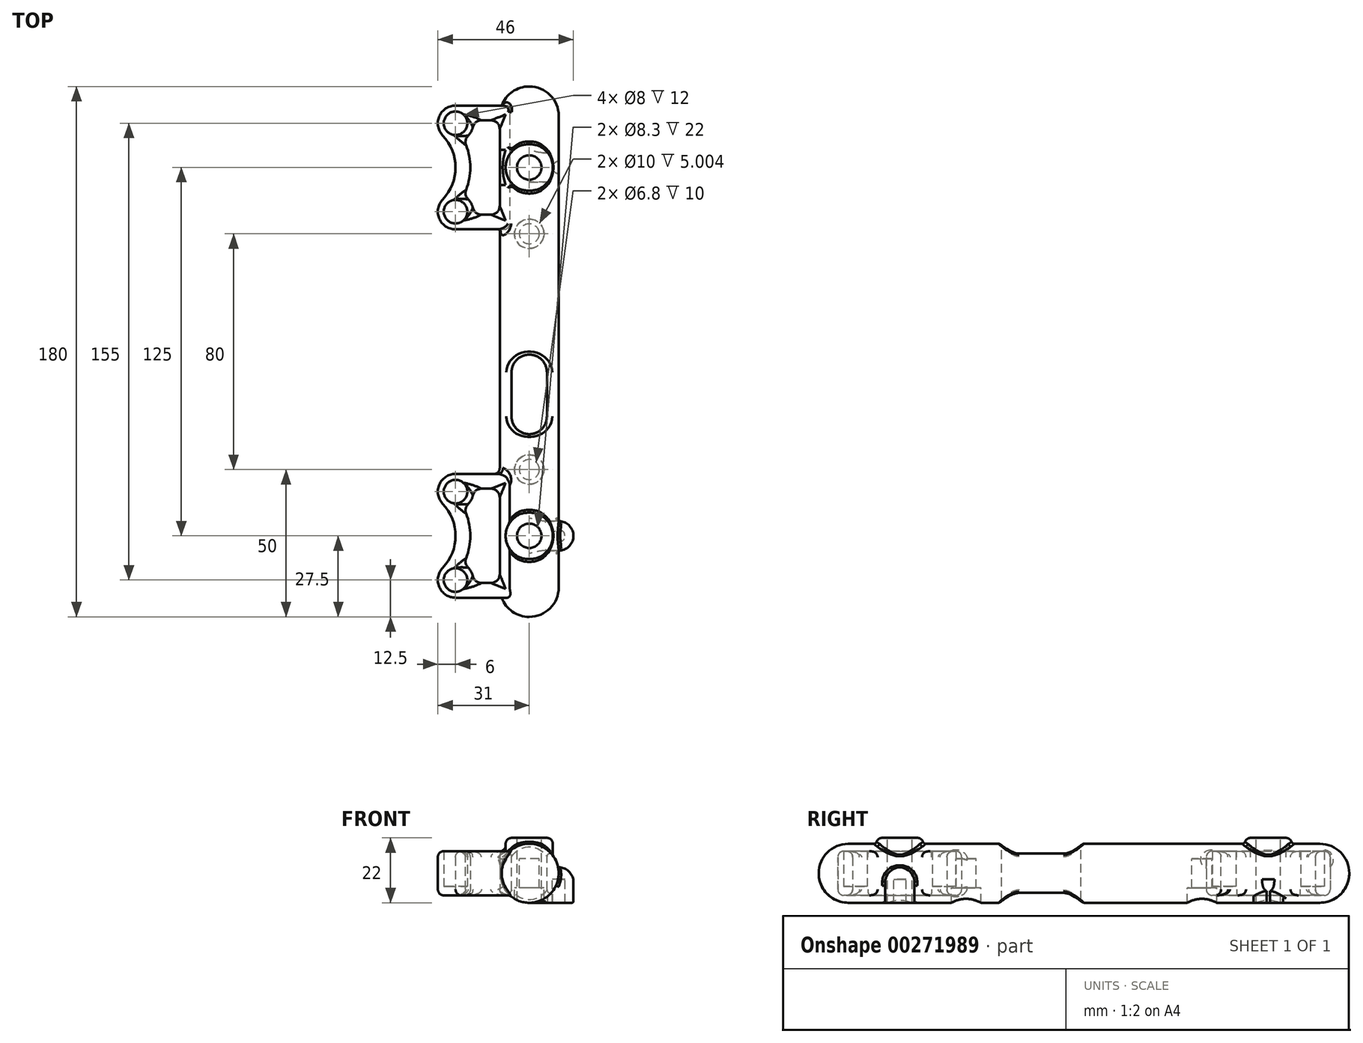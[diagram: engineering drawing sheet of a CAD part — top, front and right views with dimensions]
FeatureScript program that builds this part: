
annotation { "Feature Type Name" : "Feature", "Feature Type Description" : "" }
export const myFeature = defineFeature(function(context is Context, id is Id, definition is map)
    precondition{}
    {
        {
            var Q0;
            Q0=qCreatedBy(makeId("Front.planeOp"),FACE);
            var sketch = newSketch(context, id + "F0", { "sketchPlane" : qUnion([Q0])});
            skCircle(sketch, "E0", {"center": v(0, 0) * mm, "radius": 10 * mm});
            skSolve(sketch);
        }
        {
            var Q0;
            Q0=qCreatedBy(makeId("Right.planeOp"),FACE);
            var sketch = newSketch(context, id + "F1", { "sketchPlane" : qUnion([Q0])});
            skLineSegment(sketch, "E1", {"start": v(0, 0) * mm, "end": v(180, 0) * mm, "construction": true});
            skSolve(sketch);
        }
        {
            var Q0;
            Q0=qCreatedBy(makeId("Top.planeOp"),FACE);
            cPlane(context, id + "F2", {"entities" : qUnion([Q0]), "cplaneType" : CPlaneType.OFFSET, "offset" : 10 * mm, "oppositeDirection" : true, "width" : 150 * mm, "height" : 150 * mm});
        }
        {
            var Q0;
            Q0=qCreatedBy(id+"F2.planeOp",FACE);
            var sketch = newSketch(context, id + "F3", { "sketchPlane" : qUnion([Q0])});
            skLineSegment(sketch, "E2", {"start": v(0, 0) * mm, "end": v(0, 27.5) * mm, "construction": true});
            skLineSegment(sketch, "E3", {"start": v(0, 27.5) * mm, "end": v(0, 50) * mm, "construction": true});
            skLineSegment(sketch, "E4", {"start": v(0, 50) * mm, "end": v(0, 130) * mm, "construction": true});
            skLineSegment(sketch, "E5", {"start": v(0, 130) * mm, "end": v(0, 152.5) * mm, "construction": true});
            skCircle(sketch, "E6", {"center": v(0, 27.5) * mm, "radius": 4.15 * mm});
            skCircle(sketch, "E7", {"center": v(0, 152.5) * mm, "radius": 4.15 * mm});
            skCircle(sketch, "E8", {"center": v(0, 27.5) * mm, "radius": 8 * mm});
            skCircle(sketch, "E9", {"center": v(0, 152.5) * mm, "radius": 8 * mm});
            skCircle(sketch, "E10", {"center": v(0, 50) * mm, "radius": 3.4 * mm});
            skCircle(sketch, "E11", {"center": v(0, 130) * mm, "radius": 3.4 * mm});
            skLineSegment(sketch, "E12", {"start": v(0, 27.5) * mm, "end": v(10, 27.5) * mm, "construction": true});
            skArc(sketch, "E13", {"start": v(10, 22.5) * mm, "mid": v(15, 27.5) * mm, "end": v(10, 32.5) * mm});
            skLineSegment(sketch, "E14", {"start": v(10, 32.5) * mm, "end": v(0, 32.5) * mm});
            skLineSegment(sketch, "E15", {"start": v(10, 22.5) * mm, "end": v(0, 22.5) * mm});
            skLineSegment(sketch, "E16", {"start": v(0, 32.5) * mm, "end": v(0, 31.65) * mm});
            skLineSegment(sketch, "E17", {"start": v(0, 22.5) * mm, "end": v(0, 23.35) * mm});
            skLineSegment(sketch, "E18", {"start": v(0, 0) * mm, "end": v(-30, 0) * mm, "construction": true});
            skLineSegment(sketch, "E19", {"start": v(-30, 0) * mm, "end": v(-30, 90) * mm, "construction": true});
            skLineSegment(sketch, "E20", {"start": v(-30, 90) * mm, "end": v(0, 90) * mm, "construction": true});
            skLineSegment(sketch, "E21.MirrorCS", {"start": v(10, 147.5) * mm, "end": v(0, 147.5) * mm});
            skArc(sketch, "E22.MirrorCS", {"start": v(10, 157.5) * mm, "mid": v(15, 152.5) * mm, "end": v(10, 147.5) * mm});
            skLineSegment(sketch, "E23.MirrorCS", {"start": v(10, 157.5) * mm, "end": v(0, 157.5) * mm});
            skLineSegment(sketch, "E24", {"start": v(0, 147.5) * mm, "end": v(0, 148.35) * mm});
            skLineSegment(sketch, "E25", {"start": v(0, 157.5) * mm, "end": v(0, 156.65) * mm});
            skCircle(sketch, "E26", {"center": v(10, 27.5) * mm, "radius": 2.1 * mm, "construction": true});
            skCircle(sketch, "E27", {"center": v(10, 152.5) * mm, "radius": 2.1 * mm, "construction": true});
            skLineSegment(sketch, "E28", {"start": v(0, 27.5) * mm, "end": v(-25, 27.5) * mm, "construction": true});
            skLineSegment(sketch, "E29", {"start": v(-25, 27.5) * mm, "end": v(-25, 42.5) * mm, "construction": true});
            skCircle(sketch, "E30", {"center": v(-25, 42.5) * mm, "radius": 4 * mm, "construction": true});
            skArc(sketch, "E31", {"start": v(-25, 48.5) * mm, "mid": v(-30.51, 44.86) * mm, "end": v(-29.34, 38.36) * mm});
            skCircle(sketch, "E32.MirrorC", {"center": v(-25, 12.5) * mm, "radius": 4 * mm, "construction": true});
            skArc(sketch, "E33.MirrorC", {"start": v(-25, 6.5) * mm, "mid": v(-30.51, 10.14) * mm, "end": v(-29.34, 16.64) * mm});
            skArc(sketch, "E34", {"start": v(-30, 15.99) * mm, "mid": v(-25, 27.5) * mm, "end": v(-30, 39.01) * mm});
            skPoint(sketch, "E34.first.point", {"position": v(-29.34, 38.36) * mm});
            skPoint(sketch, "E34.second.point", {"position": v(-25, 27.5) * mm});
            skPoint(sketch, "E34.third.point", {"position": v(-29.34, 16.64) * mm});
            skLineSegment(sketch, "E35", {"start": v(0, 0) * mm, "end": v(0, 6.5) * mm, "construction": true});
            skLineSegment(sketch, "E36", {"start": v(0, 6.5) * mm, "end": v(-8, 6.5) * mm, "construction": true});
            skLineSegment(sketch, "E37", {"start": v(-8, 6.5) * mm, "end": v(-8, 48.5) * mm});
            skLineSegment(sketch, "E38", {"start": v(-8, 48.5) * mm, "end": v(-25, 48.5) * mm});
            skLineSegment(sketch, "E39", {"start": v(-8, 6.5) * mm, "end": v(-25, 6.5) * mm});
            skLineSegment(sketch, "E40.0", {"start": v(-5, 6.5) * mm, "end": v(-5, 48.5) * mm});
            skLineSegment(sketch, "E41", {"start": v(-5, 6.5) * mm, "end": v(-8, 6.5) * mm});
            skLineSegment(sketch, "E42", {"start": v(-5, 48.5) * mm, "end": v(-8, 48.5) * mm});
            skSolve(sketch);
        }
        {
            var Q0;
            Q0=qCreatedBy(id+"F2.planeOp",FACE);
            cPlane(context, id + "F4", {"entities" : qUnion([Q0]), "cplaneType" : CPlaneType.OFFSET, "offset" : 20 * mm, "width" : 150 * mm, "height" : 150 * mm});
        }
        {
            var Q0;
            Q0=qCreatedBy(id+"F4.planeOp",FACE);
            var sketch = newSketch(context, id + "F5", { "sketchPlane" : qUnion([Q0])});
            skCircle(sketch, "E43.0", {"center": v(0, 27.5) * mm, "radius": 8 * mm});
            skCircle(sketch, "E44.0", {"center": v(0, 152.5) * mm, "radius": 8 * mm});
            skLineSegment(sketch, "E45", {"start": v(0, 27.5) * mm, "end": v(0, 50) * mm, "construction": true});
            skCircle(sketch, "E46", {"center": v(0, 50) * mm, "radius": 5 * mm, "construction": true});
            skLineSegment(sketch, "E47", {"start": v(0, 50) * mm, "end": v(0, 68) * mm, "construction": true});
            skArc(sketch, "E48", {"start": v(-6, 68) * mm, "mid": v(0, 62) * mm, "end": v(6, 68) * mm});
            skArc(sketch, "E49.MirrorC", {"start": v(-6, 112) * mm, "mid": v(0, 118) * mm, "end": v(6, 112) * mm});
            skLineSegment(sketch, "E50", {"start": v(-6, 68) * mm, "end": v(-6, 83) * mm});
            skLineSegment(sketch, "E51", {"start": v(6, 112) * mm, "end": v(6, 97) * mm});
            skLineSegment(sketch, "E52", {"start": v(0, 68) * mm, "end": v(0, 83) * mm, "construction": true});
            skArc(sketch, "E53", {"start": v(6, 83) * mm, "mid": v(0, 89) * mm, "end": v(-6, 83) * mm});
            skLineSegment(sketch, "E54", {"start": v(-6, 112) * mm, "end": v(6, 112) * mm, "construction": true});
            skLineSegment(sketch, "E55", {"start": v(0, 112) * mm, "end": v(0, 90) * mm, "construction": true});
            skLineSegment(sketch, "E56.0", {"start": v(-6, 90) * mm, "end": v(6, 90) * mm});
            skArc(sketch, "E57.MirrorC", {"start": v(6, 97) * mm, "mid": v(0, 91) * mm, "end": v(-6, 97) * mm});
            skLineSegment(sketch, "E58.trimOffspring", {"start": v(-6, 97) * mm, "end": v(-6, 112) * mm});
            skLineSegment(sketch, "E59.trimOffspring", {"start": v(6, 83) * mm, "end": v(6, 68) * mm});
            skSolve(sketch);
        }
        {
            var Q0;
            Q0=makeQuery(id+"F0.imprint","IMPRINT",FACE,{"disambiguationData":[TD([[makeQuery(id+"F0.imprint","IMPRINT",EDGE,{"derivedFrom":sQuery(id+"F0.wireOp",EDGE,"E0")}),1.0]])]});
            extrude(context, id + "F6", {"entities" : qUnion([Q0]), "oppositeDirection" : true, "depth" : 180 * mm});
        }
        {
            var Q0;
            Q0=makeQuery(id+"F6.opExtrude","CAP_FACE",FACE,{"disambiguationData":[OSD([sQuery(id+"F0.wireOp",EDGE,"E0")])],"isStart":true});
            var Q1;
            Q1=makeQuery(id+"F6.opExtrude","CAP_EDGE",EDGE,{"disambiguationData":[OSD([sQuery(id+"F0.wireOp",EDGE,"E0")])],"isStart":false});
            fillet(context, id + "F7", {"entities" : qUnion([Q0, Q1]), "radius" : 10 * mm, "tangentPropagation" : true, "allowEdgeOverflow" : false});
        }
        {
            var Q0;
            Q0=makeQuery(id+"F5.imprint","IMPRINT",FACE,{"disambiguationData":[TD([[makeQuery(id+"F5.imprint","IMPRINT",EDGE,{"derivedFrom":sQuery(id+"F5.wireOp",EDGE,"E43.0")}),1.0]])]});
            var Q1;
            Q1=makeQuery(id+"F5.imprint","IMPRINT",FACE,{"disambiguationData":[TD([[makeQuery(id+"F5.imprint","IMPRINT",EDGE,{"derivedFrom":sQuery(id+"F5.wireOp",EDGE,"E44.0")}),1.0]])]});
            extrude(context, id + "F8", {"entities" : qUnion([Q0, Q1]), "operationType" : NewBodyOperationType.ADD, "oppositeDirection" : true, "depth" : 10 * mm});
        }
        {
            var Q0;
            Q0=makeQuery(id+"F5.imprint","IMPRINT",FACE,{"disambiguationData":[TD([[makeQuery(id+"F5.imprint","IMPRINT",EDGE,{"derivedFrom":sQuery(id+"F5.wireOp",EDGE,"E43.0")}),1.0]])]});
            var Q1;
            Q1=makeQuery(id+"F5.imprint","IMPRINT",FACE,{"disambiguationData":[TD([[makeQuery(id+"F5.imprint","IMPRINT",EDGE,{"derivedFrom":sQuery(id+"F5.wireOp",EDGE,"E44.0")}),1.0]])]});
            extrude(context, id + "F9", {"entities" : qUnion([Q0, Q1]), "operationType" : NewBodyOperationType.ADD, "depth" : 2 * mm});
        }
        {
            var Q0;
            Q0=makeQuery(id+"F9.opExtrude","CAP_EDGE",EDGE,{"disambiguationData":[OSD([sQuery(id+"F5.wireOp",EDGE,"E43.0")])],"isStart":false});
            var Q1;
            Q1=makeQuery(id+"F9.opExtrude","CAP_FACE",FACE,{"disambiguationData":[OSD([sQuery(id+"F5.wireOp",EDGE,"E44.0")])],"isStart":false});
            fillet(context, id + "F10", {"entities" : qUnion([Q0, Q1]), "radius" : 2 * mm, "tangentPropagation" : true, "allowEdgeOverflow" : false});
        }
        {
            var Q0;
            Q0=qCreatedBy(id+"F4.planeOp",FACE);
            cPlane(context, id + "F11", {"entities" : qUnion([Q0]), "cplaneType" : CPlaneType.OFFSET, "offset" : 2 * mm, "width" : 150 * mm, "height" : 150 * mm});
        }
        {
            var Q0;
            Q0=qCreatedBy(id+"F11.planeOp",FACE);
            var sketch = newSketch(context, id + "F12", { "sketchPlane" : qUnion([Q0])});
            skCircle(sketch, "E60.0", {"center": v(0, 27.5) * mm, "radius": 4.15 * mm});
            skCircle(sketch, "E61.0", {"center": v(0, 152.5) * mm, "radius": 4.15 * mm});
            skSolve(sketch);
        }
        {
            var Q0;
            Q0=makeQuery(id+"F12.imprint","IMPRINT",FACE,{"disambiguationData":[TD([[makeQuery(id+"F12.imprint","IMPRINT",EDGE,{"derivedFrom":sQuery(id+"F12.wireOp",EDGE,"E60.0")}),1.0]])]});
            var Q1;
            Q1=makeQuery(id+"F12.imprint","IMPRINT",FACE,{"disambiguationData":[TD([[makeQuery(id+"F12.imprint","IMPRINT",EDGE,{"derivedFrom":sQuery(id+"F12.wireOp",EDGE,"E61.0")}),1.0]])]});
            extrude(context, id + "F13", {"entities" : qUnion([Q0, Q1]), "operationType" : NewBodyOperationType.REMOVE, "oppositeDirection" : true, "depth" : 25 * mm});
        }
        {
            var Q0;
            Q0=qCreatedBy(id+"F2.planeOp",FACE);
            cPlane(context, id + "F14", {"entities" : qUnion([Q0]), "cplaneType" : CPlaneType.OFFSET, "offset" : 5 * mm, "width" : 150 * mm, "height" : 150 * mm});
        }
        {
            var Q0;
            Q0=qCreatedBy(id+"F14.planeOp",FACE);
            var sketch = newSketch(context, id + "F15", { "sketchPlane" : qUnion([Q0])});
            skLineSegment(sketch, "E62", {"start": v(0, 0) * mm, "end": v(0, 50) * mm, "construction": true});
            skLineSegment(sketch, "E63", {"start": v(0, 50) * mm, "end": v(0, 130) * mm, "construction": true});
            skCircle(sketch, "E64", {"center": v(0, 50) * mm, "radius": 5 * mm});
            skCircle(sketch, "E65", {"center": v(0, 130) * mm, "radius": 5 * mm});
            skSolve(sketch);
        }
        {
            var Q0;
            Q0 = qSketchRegion(id + "F15", true);
            extrude(context, id + "F16", {"entities" : qUnion([Q0]), "operationType" : NewBodyOperationType.REMOVE, "oppositeDirection" : true, "depth" : 5 * mm});
        }
        {
            var Q0;
            Q0=qCreatedBy(id+"F14.planeOp",FACE);
            cPlane(context, id + "F17", {"entities" : qUnion([Q0]), "cplaneType" : CPlaneType.OFFSET, "offset" : 10 * mm, "width" : 150 * mm, "height" : 150 * mm});
        }
        {
            var Q0;
            Q0=qCreatedBy(id+"F17.planeOp",FACE);
            var sketch = newSketch(context, id + "F18", { "sketchPlane" : qUnion([Q0])});
            skCircle(sketch, "E66.0", {"center": v(0, 50) * mm, "radius": 3.4 * mm});
            skCircle(sketch, "E67.0", {"center": v(0, 130) * mm, "radius": 3.4 * mm});
            skSolve(sketch);
        }
        {
            var Q0;
            Q0 = qSketchRegion(id + "F18", true);
            extrude(context, id + "F19", {"entities" : qUnion([Q0]), "operationType" : NewBodyOperationType.REMOVE, "oppositeDirection" : true, "depth" : 10 * mm});
        }
        {
            var Q0;
            {var subQ0=sQuery(id+"F3.wireOp",EDGE,"E16");Q0=makeQuery(id+"F3.imprint","IMPRINT",FACE,{"disambiguationData":[TD([[makeQuery(id+"F3.imprint","IMPRINT",EDGE,{"derivedFrom":subQ0}),1.0]])]});}
            var Q1;
            {var subQ5=sQuery(id+"F3.wireOp",EDGE,"E13");Q1=makeQuery(id+"F3.imprint","IMPRINT",FACE,{"disambiguationData":[TD([[makeQuery(id+"F3.imprint","IMPRINT",EDGE,{"derivedFrom":subQ5}),1.0]])]});}
            var Q2;
            {var subQ4=sQuery(id+"F3.wireOp",EDGE,"E24");Q2=makeQuery(id+"F3.imprint","IMPRINT",FACE,{"disambiguationData":[TD([[makeQuery(id+"F3.imprint","IMPRINT",EDGE,{"derivedFrom":subQ4}),-1.0]])]});}
            var Q3;
            {var subQ5=sQuery(id+"F3.wireOp",EDGE,"E22.MirrorCS");Q3=makeQuery(id+"F3.imprint","IMPRINT",FACE,{"disambiguationData":[TD([[makeQuery(id+"F3.imprint","IMPRINT",EDGE,{"derivedFrom":subQ5}),-1.0]])]});}
            extrude(context, id + "F20", {"entities" : qUnion([Q0, Q1, Q2, Q3]), "operationType" : NewBodyOperationType.ADD, "depth" : 12 * mm});
        }
        {
            var Q0;
            Q0=makeQuery(id+"F20.opExtrude","CAP_EDGE",EDGE,{"disambiguationData":[OSD([sQuery(id+"F3.wireOp",EDGE,"E13")])],"isStart":false});
            var Q1;
            Q1=makeQuery(id+"F20.opExtrude","CAP_EDGE",EDGE,{"disambiguationData":[OSD([sQuery(id+"F3.wireOp",EDGE,"E22.MirrorCS")])],"isStart":false});
            fillet(context, id + "F21", {"entities" : qUnion([Q0, Q1]), "radius" : 5 * mm, "tangentPropagation" : true, "allowEdgeOverflow" : false});
        }
        {
            var Q0;
            {var subQ0=makeQuery(id+"F8.opExtrude","SWEPT_FACE",FACE,{"disambiguationData":[OSD([sQuery(id+"F5.wireOp",EDGE,"E43.0")])]});var subQ1=makeQuery(id+"F6.opExtrude","SWEPT_FACE",FACE,{"disambiguationData":[OSD([sQuery(id+"F0.wireOp",EDGE,"E0")])]});Q0=makeQuery(id+"F9.boolean.opBoolean","MERGE",EDGE,{"derivedFrom":[makeQuery(id+"F8.boolean.opBoolean","INTERSECT",EDGE,{"disambiguationData":[OD(0.0)],"derivedFrom":[subQ1,subQ0]}),makeQuery(id+"F8.boolean.opBoolean","INTERSECT",EDGE,{"disambiguationData":[OD(1.0)],"derivedFrom":[subQ1,subQ0]})]});}
            var Q1;
            {var subQ0=makeQuery(id+"F8.opExtrude","SWEPT_FACE",FACE,{"disambiguationData":[OSD([sQuery(id+"F5.wireOp",EDGE,"E44.0")])]});var subQ1=makeQuery(id+"F6.opExtrude","SWEPT_FACE",FACE,{"disambiguationData":[OSD([sQuery(id+"F0.wireOp",EDGE,"E0")])]});Q1=makeQuery(id+"F9.boolean.opBoolean","MERGE",EDGE,{"derivedFrom":[makeQuery(id+"F8.boolean.opBoolean","INTERSECT",EDGE,{"disambiguationData":[OD(0.0)],"derivedFrom":[subQ1,subQ0]}),makeQuery(id+"F8.boolean.opBoolean","INTERSECT",EDGE,{"disambiguationData":[OD(1.0)],"derivedFrom":[subQ1,subQ0]})]});}
            fillet(context, id + "F22", {"entities" : qUnion([Q0, Q1]), "radius" : 1 * mm, "tangentPropagation" : true, "allowEdgeOverflow" : false});
        }
        {
            var Q0;
            Q0=makeQuery(id+"F20.boolean.opBoolean","INTERSECT",EDGE,{"disambiguationData":[OD(0.0)],"derivedFrom":[makeQuery(id+"F6.opExtrude","SWEPT_FACE",FACE,{"disambiguationData":[OSD([sQuery(id+"F0.wireOp",EDGE,"E0")])]}),makeQuery(id+"F20.opExtrude","SWEPT_FACE",FACE,{"disambiguationData":[OSD([sQuery(id+"F3.wireOp",EDGE,"E14")])]})]});
            var Q1;
            Q1=makeQuery(id+"F20.boolean.opBoolean","INTERSECT",EDGE,{"disambiguationData":[OD(0.0)],"derivedFrom":[makeQuery(id+"F6.opExtrude","SWEPT_FACE",FACE,{"disambiguationData":[OSD([sQuery(id+"F0.wireOp",EDGE,"E0")])]}),makeQuery(id+"F20.opExtrude","SWEPT_FACE",FACE,{"disambiguationData":[OSD([sQuery(id+"F3.wireOp",EDGE,"E23.MirrorCS")])]})]});
            fillet(context, id + "F23", {"entities" : qUnion([Q0, Q1]), "radius" : 1 * mm, "tangentPropagation" : true, "allowEdgeOverflow" : false});
        }
        {
            var Q0;
            Q0=qCreatedBy(id+"F2.planeOp",FACE);
            cPlane(context, id + "F24", {"entities" : qUnion([Q0]), "cplaneType" : CPlaneType.OFFSET, "offset" : 8 * mm, "width" : 150 * mm, "height" : 150 * mm});
        }
        {
            var Q0;
            Q0=qCreatedBy(id+"F24.planeOp",FACE);
            var sketch = newSketch(context, id + "F25", { "sketchPlane" : qUnion([Q0])});
            skCircle(sketch, "E68.0", {"center": v(10, 27.5) * mm, "radius": 2.1 * mm});
            skCircle(sketch, "E69.0", {"center": v(10, 152.5) * mm, "radius": 2.1 * mm});
            skSolve(sketch);
        }
        {
            var Q0;
            Q0 = qSketchRegion(id + "F25", true);
            extrude(context, id + "F26", {"entities" : qUnion([Q0]), "operationType" : NewBodyOperationType.REMOVE, "oppositeDirection" : true, "depth" : 25 * mm});
        }
        {
            var Q0;
            Q0=makeQuery(id+"F20.opExtrude","CAP_EDGE",EDGE,{"disambiguationData":[OSD([sQuery(id+"F3.wireOp",EDGE,"E22.MirrorCS")])],"isStart":true});
            var Q1;
            Q1=makeQuery(id+"F20.opExtrude","CAP_EDGE",EDGE,{"disambiguationData":[OSD([sQuery(id+"F3.wireOp",EDGE,"E13")])],"isStart":true});
            fillet(context, id + "F27", {"entities" : qUnion([Q0, Q1]), "radius" : .5 * mm, "tangentPropagation" : true, "allowEdgeOverflow" : false});
        }
        {
            var Q0;
            Q0=makeQuery(id+"F5.imprint","IMPRINT",FACE,{"disambiguationData":[TD([[makeQuery(id+"F5.imprint","IMPRINT",EDGE,{"derivedFrom":sQuery(id+"F5.wireOp",EDGE,"E49.MirrorC")}),-1.0]])]});
            var Q1;
            Q1=makeQuery(id+"F5.imprint","IMPRINT",FACE,{"disambiguationData":[TD([[makeQuery(id+"F5.imprint","IMPRINT",EDGE,{"derivedFrom":sQuery(id+"F5.wireOp",EDGE,"E48")}),1.0]])]});
            extrude(context, id + "F28", {"entities" : qUnion([Q0, Q1]), "operationType" : NewBodyOperationType.REMOVE, "oppositeDirection" : true, "depth" : 20 * mm});
        }
        {
            var Q0;
            Q0=makeQuery(id+"F28.boolean.opBoolean","INTERSECT",EDGE,{"disambiguationData":[OD(1.0)],"derivedFrom":[makeQuery(id+"F6.opExtrude","SWEPT_FACE",FACE,{"disambiguationData":[OSD([sQuery(id+"F0.wireOp",EDGE,"E0")])]}),makeQuery(id+"F28.opExtrude","SWEPT_FACE",FACE,{"disambiguationData":[OSD([sQuery(id+"F5.wireOp",EDGE,"E51")])]})]});
            var Q1;
            Q1=makeQuery(id+"F28.boolean.opBoolean","INTERSECT",EDGE,{"disambiguationData":[OD(1.0)],"derivedFrom":[makeQuery(id+"F6.opExtrude","SWEPT_FACE",FACE,{"disambiguationData":[OSD([sQuery(id+"F0.wireOp",EDGE,"E0")])]}),makeQuery(id+"F28.opExtrude","SWEPT_FACE",FACE,{"disambiguationData":[OSD([sQuery(id+"F5.wireOp",EDGE,"E59.trimOffspring")])]})]});
            var Q2;
            Q2=makeQuery(id+"F28.boolean.opBoolean","INTERSECT",EDGE,{"disambiguationData":[OD(0.0)],"derivedFrom":[makeQuery(id+"F6.opExtrude","SWEPT_FACE",FACE,{"disambiguationData":[OSD([sQuery(id+"F0.wireOp",EDGE,"E0")])]}),makeQuery(id+"F28.opExtrude","SWEPT_FACE",FACE,{"disambiguationData":[OSD([sQuery(id+"F5.wireOp",EDGE,"E49.MirrorC")])]})]});
            var Q3;
            Q3=makeQuery(id+"F28.boolean.opBoolean","INTERSECT",EDGE,{"disambiguationData":[OD(0.0)],"derivedFrom":[makeQuery(id+"F6.opExtrude","SWEPT_FACE",FACE,{"disambiguationData":[OSD([sQuery(id+"F0.wireOp",EDGE,"E0")])]}),makeQuery(id+"F28.opExtrude","SWEPT_FACE",FACE,{"disambiguationData":[OSD([sQuery(id+"F5.wireOp",EDGE,"E53")])]})]});
            fillet(context, id + "F29", {"entities" : qUnion([Q0, Q1, Q2, Q3]), "radius" : 1 * mm, "tangentPropagation" : true, "allowEdgeOverflow" : false});
        }
        {
            var Q0;
            Q0=qCreatedBy(id+"F2.planeOp",FACE);
            cPlane(context, id + "F30", {"entities" : qUnion([Q0]), "cplaneType" : CPlaneType.OFFSET, "offset" : 2.5 * mm, "width" : 150 * mm, "height" : 150 * mm});
        }
        {
            var Q0;
            Q0=qCreatedBy(id+"F30.planeOp",FACE);
            var sketch = newSketch(context, id + "F31", { "sketchPlane" : qUnion([Q0])});
            skLineSegment(sketch, "E70.0.1", {"start": v(-8, 48.5) * mm, "end": v(-25, 48.5) * mm});
            skArc(sketch, "E70.0.2", {"start": v(-25, 48.5) * mm, "mid": v(-30.51, 44.86) * mm, "end": v(-29.34, 38.36) * mm});
            skArc(sketch, "E70.0.3", {"start": v(-29.34, 38.36) * mm, "mid": v(-25, 27.5) * mm, "end": v(-29.34, 16.64) * mm});
            skArc(sketch, "E70.0.4", {"start": v(-29.34, 16.64) * mm, "mid": v(-30.51, 10.14) * mm, "end": v(-25, 6.5) * mm});
            skLineSegment(sketch, "E70.0.5", {"start": v(-25, 6.5) * mm, "end": v(-8, 6.5) * mm});
            skLineSegment(sketch, "E71.0", {"start": v(-5, 6.5) * mm, "end": v(-5, 48.5) * mm});
            skLineSegment(sketch, "E72.0", {"start": v(-5, 6.5) * mm, "end": v(-8, 6.5) * mm});
            skLineSegment(sketch, "E73.0", {"start": v(-5, 48.5) * mm, "end": v(-8, 48.5) * mm});
            skLineSegment(sketch, "E74.MirrorCS", {"start": v(-8, 131.5) * mm, "end": v(-25, 131.5) * mm});
            skArc(sketch, "E75.MirrorCS", {"start": v(-25, 131.5) * mm, "mid": v(-30.51, 135.14) * mm, "end": v(-29.34, 141.64) * mm});
            skArc(sketch, "E76.MirrorCS", {"start": v(-29.34, 141.64) * mm, "mid": v(-25, 152.5) * mm, "end": v(-29.34, 163.36) * mm});
            skArc(sketch, "E77.MirrorCS", {"start": v(-29.34, 163.36) * mm, "mid": v(-30.51, 169.86) * mm, "end": v(-25, 173.5) * mm});
            skLineSegment(sketch, "E78.MirrorCS", {"start": v(-25, 173.5) * mm, "end": v(-8, 173.5) * mm});
            skLineSegment(sketch, "E79.MirrorCS", {"start": v(-5, 173.5) * mm, "end": v(-8, 173.5) * mm});
            skLineSegment(sketch, "E80.MirrorCS", {"start": v(-5, 173.5) * mm, "end": v(-5, 131.5) * mm});
            skLineSegment(sketch, "E81.MirrorCS", {"start": v(-5, 131.5) * mm, "end": v(-8, 131.5) * mm});
            skCircle(sketch, "E82", {"center": v(-25, 42.5) * mm, "radius": 4 * mm});
            skCircle(sketch, "E83", {"center": v(-25, 12.5) * mm, "radius": 4 * mm});
            skLineSegment(sketch, "E84.0", {"start": v(-10, 43.5) * mm, "end": v(-19.08, 43.5) * mm});
            skLineSegment(sketch, "E85.0", {"start": v(-19.08, 11.5) * mm, "end": v(-10, 11.5) * mm});
            skLineSegment(sketch, "E86.0", {"start": v(-10, 11.5) * mm, "end": v(-10, 43.5) * mm});
            skArc(sketch, "E87.0", {"start": v(-19.08, 11.5) * mm, "mid": v(-19.66, 15.24) * mm, "end": v(-22.36, 17.89) * mm});
            skArc(sketch, "E88.0", {"start": v(-22.36, 37.11) * mm, "mid": v(-20, 27.5) * mm, "end": v(-22.36, 17.89) * mm});
            skArc(sketch, "E89.trimOffspring", {"start": v(-22.36, 37.11) * mm, "mid": v(-19.66, 39.76) * mm, "end": v(-19.08, 43.5) * mm});
            skLineSegment(sketch, "E90.MirrorCS", {"start": v(-10, 136.5) * mm, "end": v(-19.08, 136.5) * mm});
            skArc(sketch, "E91.MirrorCS", {"start": v(-22.36, 142.89) * mm, "mid": v(-19.66, 140.24) * mm, "end": v(-19.08, 136.5) * mm});
            skArc(sketch, "E92.MirrorCS", {"start": v(-22.36, 142.89) * mm, "mid": v(-20, 152.5) * mm, "end": v(-22.36, 162.11) * mm});
            skArc(sketch, "E93.MirrorCS", {"start": v(-19.08, 168.5) * mm, "mid": v(-19.66, 164.76) * mm, "end": v(-22.36, 162.11) * mm});
            skLineSegment(sketch, "E94.MirrorCS", {"start": v(-19.08, 168.5) * mm, "end": v(-10, 168.5) * mm});
            skLineSegment(sketch, "E95.MirrorCS", {"start": v(-10, 168.5) * mm, "end": v(-10, 136.5) * mm});
            skSolve(sketch);
        }
        {
            var Q0;
            Q0=makeQuery(id+"F31.imprint","IMPRINT",FACE,{"disambiguationData":[TD([[makeQuery(id+"F31.imprint","IMPRINT",EDGE,{"derivedFrom":sQuery(id+"F31.wireOp",EDGE,"E70.0.1")}),1.0]])]});
            var Q1;
            Q1=makeQuery(id+"F31.imprint","IMPRINT",FACE,{"disambiguationData":[TD([[makeQuery(id+"F31.imprint","IMPRINT",EDGE,{"derivedFrom":sQuery(id+"F31.wireOp",EDGE,"E83")}),1.0]])]});
            var Q2;
            Q2=makeQuery(id+"F31.imprint","IMPRINT",FACE,{"disambiguationData":[TD([[makeQuery(id+"F31.imprint","IMPRINT",EDGE,{"derivedFrom":sQuery(id+"F31.wireOp",EDGE,"E82")}),1.0]])]});
            var Q3;
            Q3=makeQuery(id+"F31.imprint","IMPRINT",FACE,{"disambiguationData":[TD([[makeQuery(id+"F31.imprint","IMPRINT",EDGE,{"derivedFrom":sQuery(id+"F31.wireOp",EDGE,"E74.MirrorCS")}),-1.0]])]});
            extrude(context, id + "F32", {"entities" : qUnion([Q0, Q1, Q2, Q3]), "operationType" : NewBodyOperationType.ADD, "depth" : 15 * mm});
        }
        {
            var Q0;
            Q0=makeQuery(id+"F32.opExtrude","CAP_EDGE",EDGE,{"disambiguationData":[OSD([sQuery(id+"F31.wireOp",EDGE,"E70.0.5"),sQuery(id+"F31.wireOp",EDGE,"E72.0")])],"isStart":false});
            var Q1;
            Q1=makeQuery(id+"F32.opExtrude","CAP_EDGE",EDGE,{"disambiguationData":[OSD([sQuery(id+"F31.wireOp",EDGE,"E70.0.5"),sQuery(id+"F31.wireOp",EDGE,"E72.0")])],"isStart":true});
            var Q2;
            Q2=makeQuery(id+"F32.boolean.opBoolean","INTERSECT",EDGE,{"derivedFrom":[makeQuery(id+"F6.opExtrude","SWEPT_FACE",FACE,{"disambiguationData":[OSD([sQuery(id+"F0.wireOp",EDGE,"E0")])]}),makeQuery(id+"F32.opExtrude","SWEPT_FACE",FACE,{"disambiguationData":[OSD([sQuery(id+"F31.wireOp",EDGE,"E70.0.1"),sQuery(id+"F31.wireOp",EDGE,"E73.0")])]})]});
            var Q3;
            Q3=makeQuery(id+"F32.opExtrude","CAP_EDGE",EDGE,{"disambiguationData":[OSD([sQuery(id+"F31.wireOp",EDGE,"E74.MirrorCS"),sQuery(id+"F31.wireOp",EDGE,"E81.MirrorCS")])],"isStart":false});
            var Q4;
            Q4=makeQuery(id+"F32.opExtrude","CAP_EDGE",EDGE,{"disambiguationData":[OSD([sQuery(id+"F31.wireOp",EDGE,"E78.MirrorCS"),sQuery(id+"F31.wireOp",EDGE,"E79.MirrorCS")])],"isStart":true});
            var Q5;
            Q5=makeQuery(id+"F32.boolean.opBoolean","INTERSECT",EDGE,{"disambiguationData":[OD(1.0)],"derivedFrom":[makeQuery(id+"F6.opExtrude","SWEPT_FACE",FACE,{"disambiguationData":[OSD([sQuery(id+"F0.wireOp",EDGE,"E0")])]}),makeQuery(id+"F32.opExtrude","CAP_FACE",FACE,{"disambiguationData":[OSD([sQuery(id+"F31.wireOp",EDGE,"E74.MirrorCS"),sQuery(id+"F31.wireOp",EDGE,"E75.MirrorCS"),sQuery(id+"F31.wireOp",EDGE,"E76.MirrorCS"),sQuery(id+"F31.wireOp",EDGE,"E77.MirrorCS"),sQuery(id+"F31.wireOp",EDGE,"E78.MirrorCS"),sQuery(id+"F31.wireOp",EDGE,"E79.MirrorCS"),sQuery(id+"F31.wireOp",EDGE,"E80.MirrorCS"),sQuery(id+"F31.wireOp",EDGE,"E81.MirrorCS"),sQuery(id+"F31.wireOp",EDGE,"E90.MirrorCS"),sQuery(id+"F31.wireOp",EDGE,"E91.MirrorCS"),sQuery(id+"F31.wireOp",EDGE,"E92.MirrorCS"),sQuery(id+"F31.wireOp",EDGE,"E93.MirrorCS"),sQuery(id+"F31.wireOp",EDGE,"E94.MirrorCS"),sQuery(id+"F31.wireOp",EDGE,"E95.MirrorCS")])],"isStart":false})]});
            fillet(context, id + "F33", {"entities" : qUnion([Q0, Q1, Q2, Q3, Q4, Q5]), "radius" : 2 * mm, "tangentPropagation" : true, "allowEdgeOverflow" : false});
        }
        {
            var Q0;
            Q0=qCreatedBy(id+"F30.planeOp",FACE);
            cPlane(context, id + "F34", {"entities" : qUnion([Q0]), "cplaneType" : CPlaneType.OFFSET, "offset" : 3 * mm, "width" : 150 * mm, "height" : 150 * mm});
        }
        {
            var Q0;
            Q0=qCreatedBy(id+"F34.planeOp",FACE);
            var sketch = newSketch(context, id + "F35", { "sketchPlane" : qUnion([Q0])});
            skCircle(sketch, "E96.0", {"center": v(-25, 12.5) * mm, "radius": 4 * mm});
            skCircle(sketch, "E97.0", {"center": v(-25, 42.5) * mm, "radius": 4 * mm});
            skCircle(sketch, "E98.MirrorC", {"center": v(-25, 137.5) * mm, "radius": 4 * mm});
            skCircle(sketch, "E99.MirrorC", {"center": v(-25, 167.5) * mm, "radius": 4 * mm});
            skSolve(sketch);
        }
        {
            var Q0;
            Q0 = qSketchRegion(id + "F35", true);
            extrude(context, id + "F36", {"entities" : qUnion([Q0]), "operationType" : NewBodyOperationType.REMOVE, "depth" : 14 * mm});
        }
        {
            var Q0;
            Q0=makeQuery(id+"F32.opExtrude","CAP_EDGE",EDGE,{"disambiguationData":[OSD([sQuery(id+"F31.wireOp",EDGE,"E86.0")])],"isStart":false});
            var Q1;
            Q1=makeQuery(id+"F32.opExtrude","CAP_EDGE",EDGE,{"disambiguationData":[OSD([sQuery(id+"F31.wireOp",EDGE,"E84.0")])],"isStart":false});
            var Q2;
            Q2=makeQuery(id+"F32.opExtrude","CAP_EDGE",EDGE,{"disambiguationData":[OSD([sQuery(id+"F31.wireOp",EDGE,"E89.trimOffspring")])],"isStart":false});
            var Q3;
            Q3=makeQuery(id+"F32.opExtrude","CAP_EDGE",EDGE,{"disambiguationData":[OSD([sQuery(id+"F31.wireOp",EDGE,"E88.0")])],"isStart":false});
            var Q4;
            Q4=makeQuery(id+"F32.opExtrude","CAP_EDGE",EDGE,{"disambiguationData":[OSD([sQuery(id+"F31.wireOp",EDGE,"E85.0")])],"isStart":false});
            var Q5;
            Q5=makeQuery(id+"F32.opExtrude","CAP_EDGE",EDGE,{"disambiguationData":[OSD([sQuery(id+"F31.wireOp",EDGE,"E87.0")])],"isStart":false});
            var Q6;
            Q6=makeQuery(id+"F32.opExtrude","CAP_EDGE",EDGE,{"disambiguationData":[OSD([sQuery(id+"F31.wireOp",EDGE,"E94.MirrorCS")])],"isStart":false});
            var Q7;
            Q7=makeQuery(id+"F32.opExtrude","CAP_EDGE",EDGE,{"disambiguationData":[OSD([sQuery(id+"F31.wireOp",EDGE,"E95.MirrorCS")])],"isStart":false});
            var Q8;
            Q8=makeQuery(id+"F32.opExtrude","CAP_EDGE",EDGE,{"disambiguationData":[OSD([sQuery(id+"F31.wireOp",EDGE,"E90.MirrorCS")])],"isStart":false});
            var Q9;
            Q9=makeQuery(id+"F32.opExtrude","CAP_EDGE",EDGE,{"disambiguationData":[OSD([sQuery(id+"F31.wireOp",EDGE,"E91.MirrorCS")])],"isStart":false});
            var Q10;
            Q10=makeQuery(id+"F32.opExtrude","CAP_EDGE",EDGE,{"disambiguationData":[OSD([sQuery(id+"F31.wireOp",EDGE,"E92.MirrorCS")])],"isStart":false});
            var Q11;
            Q11=makeQuery(id+"F32.opExtrude","CAP_EDGE",EDGE,{"disambiguationData":[OSD([sQuery(id+"F31.wireOp",EDGE,"E93.MirrorCS")])],"isStart":false});
            var Q12;
            Q12=makeQuery(id+"F32.opExtrude","CAP_EDGE",EDGE,{"disambiguationData":[OSD([sQuery(id+"F31.wireOp",EDGE,"E85.0")])],"isStart":true});
            var Q13;
            Q13=makeQuery(id+"F32.opExtrude","CAP_EDGE",EDGE,{"disambiguationData":[OSD([sQuery(id+"F31.wireOp",EDGE,"E87.0")])],"isStart":true});
            var Q14;
            Q14=makeQuery(id+"F32.opExtrude","CAP_EDGE",EDGE,{"disambiguationData":[OSD([sQuery(id+"F31.wireOp",EDGE,"E88.0")])],"isStart":true});
            var Q15;
            Q15=makeQuery(id+"F32.opExtrude","CAP_EDGE",EDGE,{"disambiguationData":[OSD([sQuery(id+"F31.wireOp",EDGE,"E89.trimOffspring")])],"isStart":true});
            var Q16;
            Q16=makeQuery(id+"F32.opExtrude","CAP_EDGE",EDGE,{"disambiguationData":[OSD([sQuery(id+"F31.wireOp",EDGE,"E84.0")])],"isStart":true});
            var Q17;
            Q17=makeQuery(id+"F32.opExtrude","CAP_EDGE",EDGE,{"disambiguationData":[OSD([sQuery(id+"F31.wireOp",EDGE,"E86.0")])],"isStart":true});
            var Q18;
            Q18=makeQuery(id+"F32.opExtrude","CAP_EDGE",EDGE,{"disambiguationData":[OSD([sQuery(id+"F31.wireOp",EDGE,"E91.MirrorCS")])],"isStart":true});
            var Q19;
            Q19=makeQuery(id+"F32.opExtrude","CAP_EDGE",EDGE,{"disambiguationData":[OSD([sQuery(id+"F31.wireOp",EDGE,"E90.MirrorCS")])],"isStart":true});
            var Q20;
            Q20=makeQuery(id+"F32.opExtrude","CAP_EDGE",EDGE,{"disambiguationData":[OSD([sQuery(id+"F31.wireOp",EDGE,"E95.MirrorCS")])],"isStart":true});
            var Q21;
            Q21=makeQuery(id+"F32.opExtrude","CAP_EDGE",EDGE,{"disambiguationData":[OSD([sQuery(id+"F31.wireOp",EDGE,"E94.MirrorCS")])],"isStart":true});
            var Q22;
            Q22=makeQuery(id+"F32.opExtrude","CAP_EDGE",EDGE,{"disambiguationData":[OSD([sQuery(id+"F31.wireOp",EDGE,"E93.MirrorCS")])],"isStart":true});
            var Q23;
            Q23=makeQuery(id+"F32.opExtrude","CAP_EDGE",EDGE,{"disambiguationData":[OSD([sQuery(id+"F31.wireOp",EDGE,"E92.MirrorCS")])],"isStart":true});
            fillet(context, id + "F37", {"entities" : qUnion([Q0, Q1, Q2, Q3, Q4, Q5, Q6, Q7, Q8, Q9, Q10, Q11, Q12, Q13, Q14, Q15, Q16, Q17, Q18, Q19, Q20, Q21, Q22, Q23]), "radius" : 2 * mm, "tangentPropagation" : true, "allowEdgeOverflow" : false});
        }
        {
            var Q0;
            Q0=makeQuery(id+"F32.opExtrude","SWEPT_EDGE",EDGE,{"disambiguationData":[OSD([sQuery(id+"F31.wireOp",EDGE,"E90.MirrorCS"),sQuery(id+"F31.wireOp",EDGE,"E95.MirrorCS")])]});
            var Q1;
            Q1=makeQuery(id+"F32.opExtrude","SWEPT_EDGE",EDGE,{"disambiguationData":[OSD([sQuery(id+"F31.wireOp",EDGE,"E90.MirrorCS"),sQuery(id+"F31.wireOp",EDGE,"E91.MirrorCS")])]});
            var Q2;
            Q2=makeQuery(id+"F32.opExtrude","SWEPT_EDGE",EDGE,{"disambiguationData":[OSD([sQuery(id+"F31.wireOp",EDGE,"E91.MirrorCS"),sQuery(id+"F31.wireOp",EDGE,"E92.MirrorCS")])]});
            var Q3;
            Q3=makeQuery(id+"F32.opExtrude","SWEPT_EDGE",EDGE,{"disambiguationData":[OSD([sQuery(id+"F31.wireOp",EDGE,"E92.MirrorCS"),sQuery(id+"F31.wireOp",EDGE,"E93.MirrorCS")])]});
            var Q4;
            Q4=makeQuery(id+"F32.opExtrude","SWEPT_EDGE",EDGE,{"disambiguationData":[OSD([sQuery(id+"F31.wireOp",EDGE,"E93.MirrorCS"),sQuery(id+"F31.wireOp",EDGE,"E94.MirrorCS")])]});
            var Q5;
            Q5=makeQuery(id+"F32.opExtrude","SWEPT_EDGE",EDGE,{"disambiguationData":[OSD([sQuery(id+"F31.wireOp",EDGE,"E94.MirrorCS"),sQuery(id+"F31.wireOp",EDGE,"E95.MirrorCS")])]});
            var Q6;
            Q6=makeQuery(id+"F32.opExtrude","SWEPT_EDGE",EDGE,{"disambiguationData":[OSD([sQuery(id+"F31.wireOp",EDGE,"E84.0"),sQuery(id+"F31.wireOp",EDGE,"E86.0")])]});
            var Q7;
            Q7=makeQuery(id+"F32.opExtrude","SWEPT_EDGE",EDGE,{"disambiguationData":[OSD([sQuery(id+"F31.wireOp",EDGE,"E85.0"),sQuery(id+"F31.wireOp",EDGE,"E86.0")])]});
            var Q8;
            Q8=makeQuery(id+"F32.opExtrude","SWEPT_EDGE",EDGE,{"disambiguationData":[OSD([sQuery(id+"F31.wireOp",EDGE,"E85.0"),sQuery(id+"F31.wireOp",EDGE,"E87.0")])]});
            var Q9;
            Q9=makeQuery(id+"F32.opExtrude","SWEPT_EDGE",EDGE,{"disambiguationData":[OSD([sQuery(id+"F31.wireOp",EDGE,"E87.0"),sQuery(id+"F31.wireOp",EDGE,"E88.0")])]});
            var Q10;
            Q10=makeQuery(id+"F32.opExtrude","SWEPT_EDGE",EDGE,{"disambiguationData":[OSD([sQuery(id+"F31.wireOp",EDGE,"E88.0"),sQuery(id+"F31.wireOp",EDGE,"E89.trimOffspring")])]});
            var Q11;
            Q11=makeQuery(id+"F32.opExtrude","SWEPT_EDGE",EDGE,{"disambiguationData":[OSD([sQuery(id+"F31.wireOp",EDGE,"E84.0"),sQuery(id+"F31.wireOp",EDGE,"E89.trimOffspring")])]});
            fillet(context, id + "F38", {"entities" : qUnion([Q0, Q1, Q2, Q3, Q4, Q5, Q6, Q7, Q8, Q9, Q10, Q11]), "radius" : 3 * mm, "tangentPropagation" : true, "allowEdgeOverflow" : false});
        }
    });
